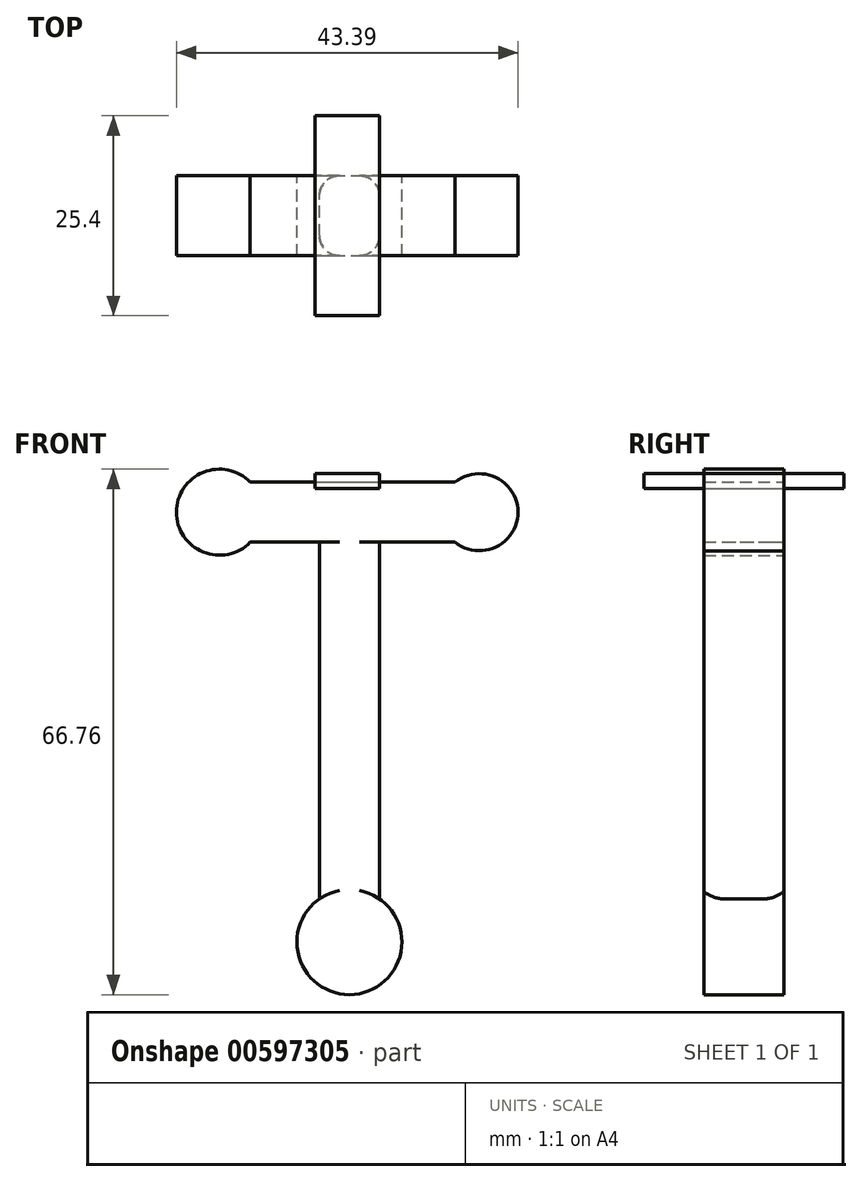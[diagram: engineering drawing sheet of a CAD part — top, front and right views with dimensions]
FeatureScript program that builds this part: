
annotation { "Feature Type Name" : "Feature", "Feature Type Description" : "" }
export const myFeature = defineFeature(function(context is Context, id is Id, definition is map)
    precondition{}
    {
        {
            var Q0;
            Q0=qCreatedBy(makeId("Front.planeOp"),FACE);
            var sketch = newSketch(context, id + "F0", { "sketchPlane" : qUnion([Q0])});
            skLineSegment(sketch, "E0.bottom", {"start": v(0.54, 0) * mm, "end": v(8.16, 0) * mm});
            skLineSegment(sketch, "E0.top", {"start": v(0.54, -50.8) * mm, "end": v(8.16, -50.8) * mm});
            skLineSegment(sketch, "E0.left", {"start": v(0.54, 0) * mm, "end": v(0.54, -50.8) * mm});
            skLineSegment(sketch, "E0.right", {"start": v(8.16, 0) * mm, "end": v(8.16, -50.8) * mm});
            skLineSegment(sketch, "E1.bottom", {"start": v(-12.16, 7.62) * mm, "end": v(20.86, 7.62) * mm});
            skLineSegment(sketch, "E1.top", {"start": v(-12.16, 0) * mm, "end": v(20.86, 0) * mm});
            skLineSegment(sketch, "E1.left", {"start": v(-12.16, 7.62) * mm, "end": v(-12.16, 0) * mm});
            skLineSegment(sketch, "E1.right", {"start": v(20.86, 7.62) * mm, "end": v(20.86, 0) * mm});
            skCircle(sketch, "E2", {"center": v(20.86, 3.81) * mm, "radius": 4.9 * mm});
            skCircle(sketch, "E3", {"center": v(-12.16, 3.81) * mm, "radius": 5.47 * mm});
            skCircle(sketch, "E4", {"center": v(4.35, -50.8) * mm, "radius": 6.68 * mm});
            skSolve(sketch);
        }
        {
            var Q0;
            Q0 = qSketchRegion(id + "F0", true);
            extrude(context, id + "F1", {"entities" : qUnion([Q0]), "endBound" : BoundingType.SYMMETRIC, "depth" : 10.16 * mm, "offsetDistance" : 25.4 * mm});
        }
        {
            var Q0;
            Q0=makeQuery(id+"F1.opExtrude","CAP_EDGE",EDGE,{"disambiguationData":[OSD([sQuery(id+"F0.wireOp",EDGE,"E0.right")])],"isStart":false});
            var Q1;
            Q1=makeQuery(id+"F1.opExtrude","CAP_EDGE",EDGE,{"disambiguationData":[OSD([sQuery(id+"F0.wireOp",EDGE,"E0.left")])],"isStart":false});
            var Q2;
            Q2=makeQuery(id+"F1.opExtrude","CAP_EDGE",EDGE,{"disambiguationData":[OSD([sQuery(id+"F0.wireOp",EDGE,"E0.left")])],"isStart":true});
            var Q3;
            Q3=makeQuery(id+"F1.opExtrude","CAP_EDGE",EDGE,{"disambiguationData":[OSD([sQuery(id+"F0.wireOp",EDGE,"E0.right")])],"isStart":true});
            fillet(context, id + "F2", {"entities" : qUnion([Q0, Q1, Q2, Q3]), "radius" : 2.54 * mm, "tangentPropagation" : true, "allowEdgeOverflow" : false});
        }
        {
            var Q0;
            Q0=qCreatedBy(makeId("Front.planeOp"),FACE);
            var sketch = newSketch(context, id + "F3", { "sketchPlane" : qUnion([Q0])});
            skLineSegment(sketch, "E5", {"start": v(0, 59.5) * mm, "end": v(3.84, 71.2) * mm});
            skLineSegment(sketch, "E6", {"start": v(3.84, 71.2) * mm, "end": v(8.19, 59.5) * mm});
            skLineSegment(sketch, "E7", {"start": v(8.19, 59.32) * mm, "end": v(8.19, 8.52) * mm});
            skLineSegment(sketch, "E8", {"start": v(0, 59.5) * mm, "end": v(0, 8.7) * mm});
            skLineSegment(sketch, "E9", {"start": v(0, 8.7) * mm, "end": v(8.19, 8.52) * mm});
            skLineSegment(sketch, "E10.bottom", {"start": v(0, 8.7) * mm, "end": v(8.19, 8.7) * mm});
            skLineSegment(sketch, "E10.top", {"start": v(0, 6.83) * mm, "end": v(8.19, 6.83) * mm});
            skLineSegment(sketch, "E10.left", {"start": v(0, 8.7) * mm, "end": v(0, 6.83) * mm});
            skLineSegment(sketch, "E10.right", {"start": v(8.19, 8.7) * mm, "end": v(8.19, 6.83) * mm});
            skSolve(sketch);
        }
        {
            var Q0;
            Q0 = qSketchRegion(id + "F3", true);
            extrude(context, id + "F4", {"entities" : qUnion([Q0]), "endBound" : BoundingType.SYMMETRIC, "depth" : 25.4 * mm, "offsetDistance" : 25.4 * mm});
        }
    });
